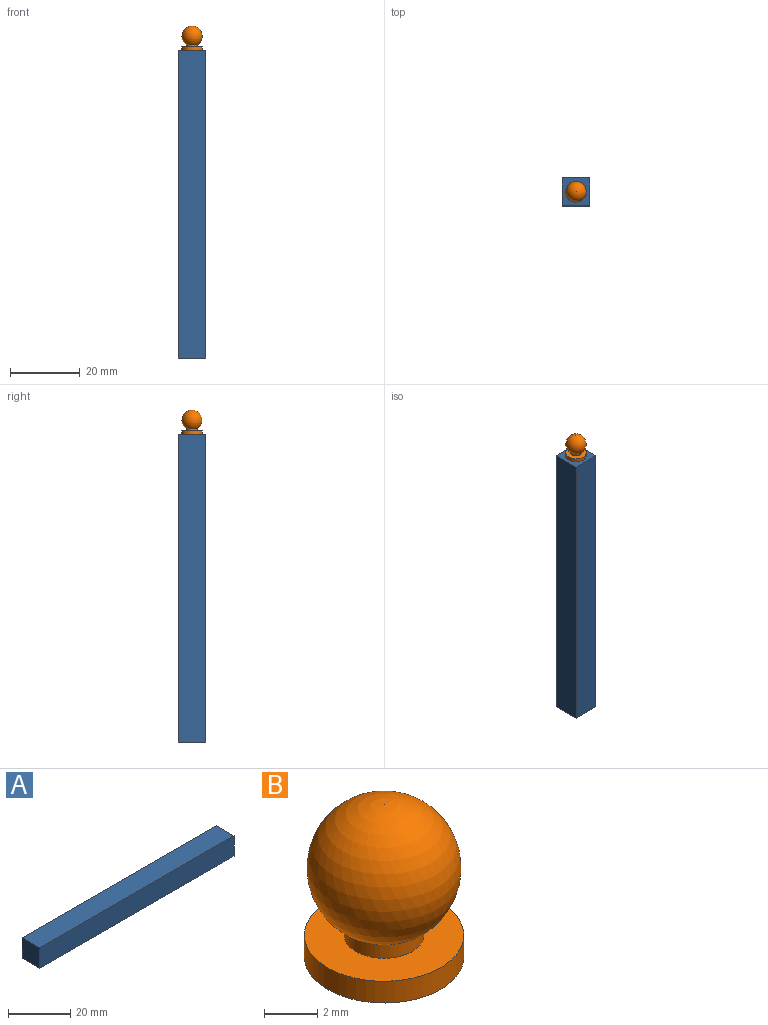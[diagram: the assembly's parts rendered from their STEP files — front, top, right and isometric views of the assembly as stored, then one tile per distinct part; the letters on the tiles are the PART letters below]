
ASSEMBLY  parts=2 mates=1
PART A: 6 faces, bbox 88x8x8 mm
  f0: plane 88x8mm, normal (0,0,-1), area 704mm2, adj f1,f3,f4,f5
  f1: plane 8x8mm, normal (1,0,0), area 64mm2, adj f0,f2,f4,f5
  f2: plane 88x8mm, normal (0,0,1), area 704mm2, adj f1,f3,f4,f5
  f3: plane 8x8mm, normal (-1,0,0), area 64mm2, adj f0,f2,f4,f5
  f4: plane 88x8mm, normal (0,-1,0), area 704mm2, adj f0,f1,f2,f3
  f5: plane 88x8mm, normal (0,1,0), area 704mm2, adj f0,f1,f2,f3
PART B: 5 faces, bbox 6x6x7 mm
  f0: plane 6x6mm, normal (0,0,-1), area 28.3mm2, adj f4
  f1: sphere r=2.9mm, area 98.1mm2, adj f2
  f2: cylinder r=1.5mm len=3mm, axis (0,0,1), area 5.8mm2, adj f1,f3
  f3: plane 6x6mm, normal (0,0,1), area 21.2mm2, adj f2,f4
  f4: cylinder r=3mm len=6mm, axis (0,0,1), area 18.8mm2, adj f0,f3
PLACE A rot(axis=(0,1,0),90deg) t=(-3.98,-0.04,-3.59)mm
PLACE B t=(0.02,-0.04,40.41)mm
MATE fastened B.f2 <-> A.f3  axis (0,0,-1) through (0.02,-0.04,40.41)mm
